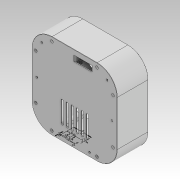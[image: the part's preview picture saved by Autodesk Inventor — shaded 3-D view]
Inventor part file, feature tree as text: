
AUTODESK INVENTOR PART (.ipt)
format: ipt  version: 2020 (Build 240168000, 168)  size: 794,624 bytes
history: native  units: mm
features: sketch x23, extrude x19, projected_geometry x7, other x4, plane x4, chamfer x2, loft x1, fillet x1
ambient origin geometry x8: Origin, YZ Plane, XZ Plane, XY Plane, X Axis, Y Axis, Z Axis, Center Point
bodies: Solid1 (feature_tree)
feature tree (61):
  other  "Blocks"
  sketch  "Sketch1"  dims[d1=170.0mm d2=170.0mm]
  extrude  "Extrusion1"  Depth=170.0mm
  extrude  "Extrusion2"  Depth=62.0mm TaperAngle=0.0deg
  plane  "Work Plane1"
  loft  "Loft1"
  extrude  "Extrusion3"  Depth=7.5mm
  plane  "Work Plane2"
  sketch  "Sketch6"  dims[d14=17.5mm d15=7.5mm]
  plane  "Work Plane3"
  sketch  "Sketch7"  dims[d16=10.0mm d17=65.0mm]
  extrude  "Extrusion4"  Depth=7.5mm
  extrude  "Extrusion5"  Depth=7.5mm
  extrude  "Extrusion7"  Depth=10.0mm
  extrude  "Extrusion8"  Depth=7.5mm
  extrude  "SnipSnip"  TaperAngle=0.0deg  [1 undecoded]
  extrude  "Extrusion10"  Depth=5.0mm TaperAngle=0.0deg
  extrude  "Extrusion11"  [1 undecoded]
  extrude  "Extrusion12"  Depth=2.5mm
  extrude  "Extrusion14"  Depth=10.0mm
  plane  "Work Plane4"
  extrude  "Extrusion15"  Depth=77.0mm TaperAngle=0.0deg
  extrude  "Extrusion16"  Depth=10.0mm
  extrude  "Extrusion17"  Depth=10.0mm TaperAngle=0.0deg
  extrude  "Extrusion18"  TaperAngle=45.0deg  [1 undecoded]
  extrude  "Extrusion19"  Depth=40.0mm TaperAngle=360.0deg
  extrude  "Extrusion20"  TaperAngle=0.0deg  [1 undecoded]
  sketch  "Sketch26"  dims[d72=35.0mm]
  extrude  "Extrusion21"  Depth=21.0mm
  chamfer  "Chamfer1"  Distance=55.0mm
  fillet  "Fillet1"  Radius=15.0mm
  chamfer  "Chamfer2"  Distance=74.1mm
  sketch  "Sketch27"  dims[d73=8.0mm d92=55.0mm d93=15.0mm d94=74.1mm d95=52.0mm d96=2.4mm d97=45.0mm d99=6.0mm d100=7.0mm d101=0.0mm d102=26.0mm d103=57.0mm d104=47.0mm d105=28.0mm d106=4.5mm d107=40.0mm d108=5.0mm d109=0.0mm d110=56.2mm d111=60.0deg d112=3.0mm d113=0.0mm d114=3.0mm d115=0.0mm d116=75.0mm d117=92.0mm d118=3.8mm d119=15.0mm d120=0.0mm d121=0.0mm d122=15.0mm d123=7.2mm d124=2.5mm d125=0.0mm d126=32.0mm d127=10.0mm d128=0.0mm d129=35.0mm d131=14.0mm d132=13.0mm d134=12.0mm d135=8.0mm d136=28.0mm d137=0.0mm d139=0.5mm d140=2.0mm d141=45.0deg d142=5.0mm d143=1.0mm d145=0.0mm d146=0.5mm d147=2.0mm d148=45.0deg d149=1.0mm d150=1.0mm d151=14.0mm d152=2.0mm]
  sketch  "Sketch2"  dims[d3=40.0mm d4=62.0mm d5=0.0mm]
  other  "Block1"
  sketch  "Sketch3"  dims[d7=0.0mm d8=0.0mm d9=5.5mm]
  sketch  "Sketch4"  dims[d10=57.5mm d11=7.5mm]
  projected_geometry  "Projected Loop1"
  sketch  "Sketch5"  dims[d12=7.5mm d13=7.5mm]
  projected_geometry  "Projected Loop2"
  projected_geometry  "Projected Loop3"
  projected_geometry  "Projected Loop4"
  sketch  "Sketch8"  dims[d18=7.5mm d19=7.5mm]
  sketch  "Sketch10"  dims[d20=15.0mm d21=0.0mm d22=90.0deg]
  sketch  "Sketch11"  dims[d23=0.0mm d24=90.0deg d25=5.0mm d26=0.0mm]
  sketch  "Sketch12"  dims[d27=175.0mm d28=-1.5mm]
  sketch  "Sketch13"  dims[d29=2.5mm d30=4.0mm]
  sketch  "Sketch14"  dims[d31=10.0mm d32=0.0mm d33=145.0mm]
  projected_geometry  "Projected Loop5"
  sketch  "Sketch15"  dims[d34=29.75mm d35=0.0mm d41=77.0mm d42=0.0mm]
  sketch  "Sketch18"  dims[d44=2.5mm d45=60.0mm d47=10.0mm d48=10.0mm d50=10.0mm]
  sketch  "Sketch19"  dims[d52=10.0mm d53=0.0mm d54=60.0mm d55=0.0mm]
  sketch  "Sketch20"  dims[d56=10.0mm d57=0.0mm d59=45.0deg]
  projected_geometry  "Projected Loop6"
  sketch  "Sketch21"  dims[d60=5.5mm d61=40.0mm d63=360.0deg]
  sketch  "Sketch22"  dims[d65=10.0mm d66=0.0mm d67=0.0mm d68=0.0mm]
  sketch  "Sketch23"  dims[d69=9.6mm d70=21.0mm]
  sketch  "Sketch24"  dims[d71=1.0mm]
  projected_geometry  "Projected Loop7"
  other  "Block1:1"
  other  "Block1:2"
note: 4 required parameter values undecoded (feature->parameter linkage not recoverable at this tier; creation-order binding heuristic only, values carry confidence <= 0.55)
